# Revit family: Partition-4_Panels_High-Skyfold_Classic_Zenith-7-0_to_8-0_FC_2150_to_2440
name_source: partatom
category: Generic Models
units: mm (PartAtom-declared; Revit-internal decimal feet)

## family parameters
Always vertical = Yes
Can host rebar = No
Cut with Voids When Loaded = No
Host = Ceiling
Maintain Annotation Orientation = No
Part Type = Normal
Room Calculation Point = No
Round Connector Dimension = Use Diameter
Shared = No

## types (3) — shared parameters
Default Elevation = 0' - 0"
Description = Custom Powerlift Partitions
Distance From Acoustic Barrier = 0' - 2"
Manufacturer = Skyfold
Model = Compact Drive System
Pocket Depth"D" = 1' - 2 1/2"
URL = http://www.skyfold.com
Wall Thickness = 0' - 11 3/4"

## per-type parameters (varying)
| type | Acoustic Barrier"C" | Beam Height"B" | Panel Height"F" | Pocket Width"E" | Total Panel Height |
| 7' - 0" | 8' - 2 1/2" | 9' - 2 1/4" | 1' - 11 1/2" | 4' - 8 3/4" | 7' - 11 1/2" |
| 7' - 6" | 8' - 8 1/2" | 9' - 5 1/4" | 2' - 1" | 4' - 11 3/4" | 8' - 5 1/2" |
| 8' - 0" | 9' - 2 1/2" | 10' - 2 1/4" | 2' - 2 1/2" | 5' - 2 3/4" | 8' - 11 1/2" |

note: column(s) folded — value = type name in every type: Finished Ceiling"A"

## geometry (parser evidence)
native form markers: Sweep x24
no freeform markers — native parametric forms only
